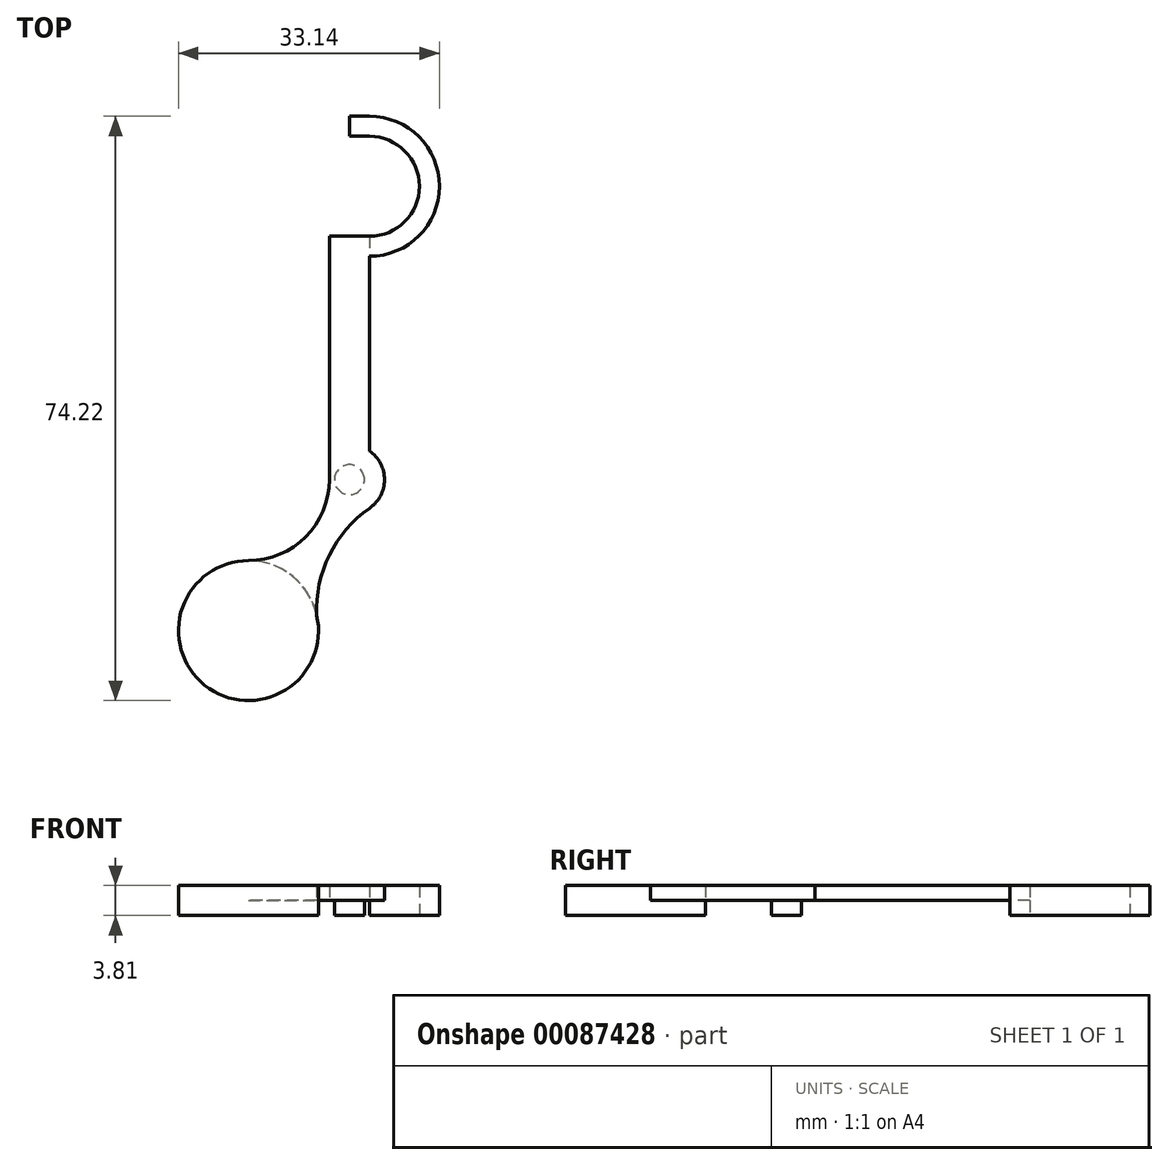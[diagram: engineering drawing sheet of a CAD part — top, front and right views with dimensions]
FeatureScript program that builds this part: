
annotation { "Feature Type Name" : "Feature", "Feature Type Description" : "" }
export const myFeature = defineFeature(function(context is Context, id is Id, definition is map)
    precondition{}
    {
        {
            var Q0;
            Q0=qCreatedBy(makeId("Top.planeOp"),FACE);
            var sketch = newSketch(context, id + "F0", { "sketchPlane" : qUnion([Q0])});
            skLineSegment(sketch, "E0", {"start": v(0, 50.8) * mm, "end": v(0, 0) * mm, "construction": true});
            skLineSegment(sketch, "E1", {"start": v(0, 35.56) * mm, "end": v(0, 0) * mm});
            skPoint(sketch, "E2", {"position": v(-31.04, 0) * mm});
            skCircle(sketch, "E3", {"center": v(-15.36, -11.99) * mm, "radius": 8.9 * mm});
            skLineSegment(sketch, "E4", {"start": v(0, 53.34) * mm, "end": v(0, 50.8) * mm});
            skArc(sketch, "E5", {"start": v(-15.36, -3.1) * mm, "mid": v(-8.1, -0.09) * mm, "end": v(-5.08, 7.19) * mm});
            skArc(sketch, "E6", {"start": v(0, 35.56) * mm, "mid": v(8.89, 44.45) * mm, "end": v(0, 53.34) * mm});
            skArc(sketch, "E7", {"start": v(0, 38.1) * mm, "mid": v(6.35, 44.45) * mm, "end": v(0, 50.8) * mm});
            skLineSegment(sketch, "E8", {"start": v(0, 38.1) * mm, "end": v(0, 35.56) * mm});
            skLineSegment(sketch, "E9", {"start": v(-5.08, 38.1) * mm, "end": v(0, 38.1) * mm});
            skLineSegment(sketch, "E10", {"start": v(-5.08, 38.1) * mm, "end": v(-5.08, 0) * mm});
            skLineSegment(sketch, "E11", {"start": v(0, 3.54) * mm, "end": v(-5.08, 0) * mm, "construction": true});
            skLineSegment(sketch, "E12", {"start": v(0, 53.34) * mm, "end": v(-2.54, 53.34) * mm});
            skLineSegment(sketch, "E13", {"start": v(-2.54, 53.34) * mm, "end": v(-2.54, 50.8) * mm});
            skLineSegment(sketch, "E14", {"start": v(-2.54, 50.8) * mm, "end": v(0, 50.8) * mm});
            skCircle(sketch, "E15", {"center": v(-2.54, 7.19) * mm, "radius": 1.9 * mm});
            skPoint(sketch, "E15.centerSnap0", {"position": v(-2.54, 1.77) * mm});
            skArc(sketch, "E16.0", {"start": v(0, 3.54) * mm, "mid": v(1.9, 7.19) * mm, "end": v(0, 10.83) * mm});
            skArc(sketch, "E17", {"start": v(0, 3.54) * mm, "mid": v(-5.5, -3.28) * mm, "end": v(-6.47, -11.99) * mm});
            skSolve(sketch);
        }
        {
            var Q0;
            Q0=qSketchRegion(id+"F0",true);
            extrude(context, id + "F1", {"entities" : qUnion([Q0]), "depth" : 3.8 * mm});
        }
        {
            var Q0;
            {var subQ1=sQuery(id+"F0.wireOp",EDGE,"E1");Q0=makeQuery(id+"F0.imprint","IMPRINT",FACE,{"disambiguationData":[TD([[makeQuery(id+"F0.imprint","IMPRINT",EDGE,{"derivedFrom":subQ1}),-1.0]])]});}
            var Q1;
            {var subQ0=sQuery(id+"F0.wireOp",EDGE,"E5");Q1=makeQuery(id+"F0.imprint","IMPRINT",FACE,{"disambiguationData":[TD([[makeQuery(id+"F0.imprint","IMPRINT",EDGE,{"derivedFrom":subQ0}),-1.0]])]});}
            var Q2;
            {var subQ0=sQuery(id+"F0.wireOp",EDGE,"t0VB1PUQ-RfSN-Wfje-U51E-yYEwLlaeleKK");Q2=makeQuery(id+"F0.imprint","IMPRINT",FACE,{"disambiguationData":[TD([[makeQuery(id+"F0.imprint","IMPRINT",EDGE,{"derivedFrom":subQ0}),1.0]])]});}
            var Q3;
            {var subQ0=sQuery(id+"F0.wireOp",EDGE,"E16.0");Q3=makeQuery(id+"F0.imprint","IMPRINT",FACE,{"disambiguationData":[TD([[makeQuery(id+"F0.imprint","IMPRINT",EDGE,{"derivedFrom":subQ0}),1.0]])]});}
            extrude(context, id + "F2", {"entities" : qUnion([Q0, Q1, Q2, Q3]), "operationType" : NewBodyOperationType.REMOVE, "depth" : 1.9 * mm});
        }
        {
            var Q0;
            Q0=makeQuery(id+"F0.imprint","IMPRINT",FACE,{"disambiguationData":[TD([[makeQuery(id+"F0.imprint","IMPRINT",EDGE,{"derivedFrom":sQuery(id+"F0.wireOp",EDGE,"E15")}),1.0]])]});
            extrude(context, id + "F3", {"entities" : qUnion([Q0]), "operationType" : NewBodyOperationType.ADD, "depth" : 3.8 * mm});
        }
    });
